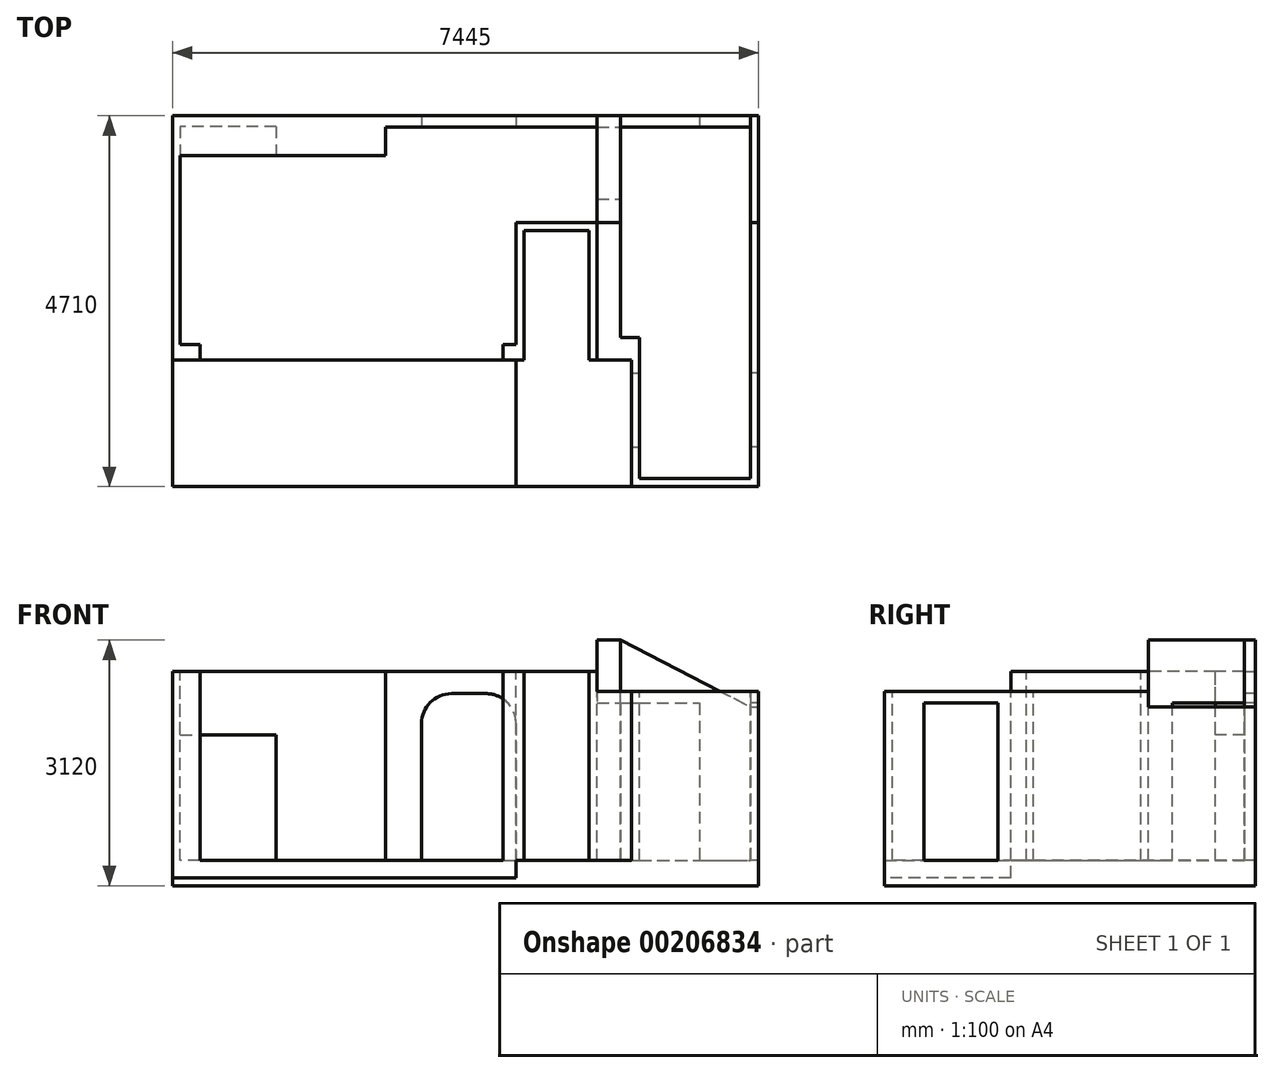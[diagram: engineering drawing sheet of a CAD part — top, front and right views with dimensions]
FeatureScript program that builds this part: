
annotation { "Feature Type Name" : "Feature", "Feature Type Description" : "" }
export const myFeature = defineFeature(function(context is Context, id is Id, definition is map)
    precondition{}
    {
        {
            var Q0;
            Q0=qCreatedBy(makeId("Top.planeOp"),FACE);
            var sketch = newSketch(context, id + "F0", { "sketchPlane" : qUnion([Q0])});
            skLineSegment(sketch, "E0.bottom", {"start": v(-1579.98, 3780.8) * mm, "end": v(5865.02, 3780.8) * mm});
            skLineSegment(sketch, "E0.top", {"start": v(-1579.98, -929.2) * mm, "end": v(5865.02, -929.2) * mm});
            skLineSegment(sketch, "E0.left", {"start": v(-1579.98, 3780.8) * mm, "end": v(-1579.98, -929.2) * mm});
            skLineSegment(sketch, "E0.right", {"start": v(5865.02, 3780.8) * mm, "end": v(5865.02, -929.2) * mm});
            skSolve(sketch);
        }
        {
            var Q0;
            Q0 = qSketchRegion(id + "F0", true);
            extrude(context, id + "F1", {"entities" : qUnion([Q0]), "depth" : 2720 * mm});
        }
        {
            var Q0;
            Q0=makeQuery(id+"F1.opExtrude","CAP_FACE",FACE,{"disambiguationData":[OSD([sQuery(id+"F0.wireOp",EDGE,"E0.bottom"),sQuery(id+"F0.wireOp",EDGE,"E0.top"),sQuery(id+"F0.wireOp",EDGE,"E0.left"),sQuery(id+"F0.wireOp",EDGE,"E0.right")])],"isStart":false});
            var sketch = newSketch(context, id + "F2", { "sketchPlane" : qUnion([Q0])});
            skLineSegment(sketch, "E1.0.0", {"start": v(5865.02, 3780.8) * mm, "end": v(-1579.98, 3780.8) * mm, "construction": true});
            skLineSegment(sketch, "E1.0.1", {"start": v(-1579.98, 3780.8) * mm, "end": v(-1579.98, -929.2) * mm, "construction": true});
            skLineSegment(sketch, "E1.0.2", {"start": v(-1579.98, -929.2) * mm, "end": v(5865.02, -929.2) * mm, "construction": true});
            skLineSegment(sketch, "E1.0.3", {"start": v(5865.02, -929.2) * mm, "end": v(5865.02, 3780.8) * mm, "construction": true});
            skLineSegment(sketch, "E2", {"start": v(-1479.98, 3275.8) * mm, "end": v(-1479.98, 875.8) * mm});
            skLineSegment(sketch, "E3", {"start": v(-1479.98, 875.8) * mm, "end": v(-1229.98, 875.8) * mm});
            skLineSegment(sketch, "E4", {"start": v(-1229.98, 875.8) * mm, "end": v(-1229.98, 675.8) * mm});
            skLineSegment(sketch, "E5", {"start": v(-1229.98, 675.8) * mm, "end": v(2620.02, 675.8) * mm});
            skLineSegment(sketch, "E6", {"start": v(2620.02, 675.8) * mm, "end": v(2620.02, 875.8) * mm});
            skLineSegment(sketch, "E7", {"start": v(2620.02, 875.8) * mm, "end": v(2785.02, 875.8) * mm});
            skLineSegment(sketch, "E8", {"start": v(2785.02, 875.8) * mm, "end": v(2785.02, 2425.8) * mm});
            skLineSegment(sketch, "E9", {"start": v(2785.02, 2425.8) * mm, "end": v(3815.02, 2425.8) * mm});
            skLineSegment(sketch, "E10", {"start": v(4115.02, 963.59) * mm, "end": v(4355.02, 963.59) * mm});
            skLineSegment(sketch, "E11", {"start": v(4355.02, 963.59) * mm, "end": v(4355.02, -829.2) * mm});
            skLineSegment(sketch, "E12", {"start": v(4355.02, -829.2) * mm, "end": v(5765.02, -829.2) * mm});
            skLineSegment(sketch, "E13", {"start": v(5765.02, -829.2) * mm, "end": v(5765.02, -429.2) * mm});
            skLineSegment(sketch, "E14", {"start": v(5765.02, -429.2) * mm, "end": v(5865.02, -429.2) * mm, "construction": true});
            skLineSegment(sketch, "E15", {"start": v(5865.02, -429.2) * mm, "end": v(5865.02, 510.8) * mm, "construction": true});
            skLineSegment(sketch, "E16", {"start": v(5865.02, 510.8) * mm, "end": v(5765.02, 510.8) * mm, "construction": true});
            skLineSegment(sketch, "E17", {"start": v(5765.02, 510.8) * mm, "end": v(5765.02, 3640.8) * mm});
            skLineSegment(sketch, "E18", {"start": v(5765.02, 3640.8) * mm, "end": v(5115.02, 3640.8) * mm});
            skLineSegment(sketch, "E19", {"start": v(5115.02, 3640.8) * mm, "end": v(5115.02, 3780.8) * mm, "construction": true});
            skLineSegment(sketch, "E20", {"start": v(5115.02, 3780.8) * mm, "end": v(4115.02, 3780.8) * mm, "construction": true});
            skLineSegment(sketch, "E21", {"start": v(4115.02, 3780.8) * mm, "end": v(4115.02, 3640.8) * mm, "construction": true});
            skLineSegment(sketch, "E22", {"start": v(4115.02, 3640.8) * mm, "end": v(2785.02, 3640.8) * mm});
            skLineSegment(sketch, "E23", {"start": v(2785.02, 3640.8) * mm, "end": v(2785.02, 3780.8) * mm});
            skLineSegment(sketch, "E24", {"start": v(2785.02, 3780.8) * mm, "end": v(1585.02, 3780.8) * mm, "construction": true});
            skLineSegment(sketch, "E25", {"start": v(1585.02, 3780.8) * mm, "end": v(1585.02, 3640.8) * mm});
            skLineSegment(sketch, "E26", {"start": v(1585.02, 3640.8) * mm, "end": v(1130.02, 3640.8) * mm});
            skLineSegment(sketch, "E27", {"start": v(1130.02, 3640.8) * mm, "end": v(1130.02, 3275.8) * mm});
            skLineSegment(sketch, "E28", {"start": v(1130.02, 3275.8) * mm, "end": v(-1479.98, 3275.8) * mm});
            skPoint(sketch, "E29.orphan", {"position": v(-1479.98, 3640.8) * mm});
            skLineSegment(sketch, "E30", {"start": v(2785.02, 3710.8) * mm, "end": v(2785.02, 1947.94) * mm, "construction": true});
            skLineSegment(sketch, "E31", {"start": v(3815.02, 2425.8) * mm, "end": v(3815.02, 2725.8) * mm});
            skLineSegment(sketch, "E32", {"start": v(3815.02, 2725.8) * mm, "end": v(4115.02, 2725.8) * mm});
            skLineSegment(sketch, "E33", {"start": v(4115.02, 2725.8) * mm, "end": v(4115.02, 963.59) * mm});
            skLineSegment(sketch, "E34", {"start": v(1585.02, 3640.8) * mm, "end": v(2785.02, 3640.8) * mm});
            skLineSegment(sketch, "E35", {"start": v(4115.02, 3640.8) * mm, "end": v(5115.02, 3640.8) * mm});
            skLineSegment(sketch, "E36", {"start": v(5765.02, 510.8) * mm, "end": v(5765.02, -429.2) * mm});
            skSolve(sketch);
        }
        {
            var Q0;
            Q0 = qSketchRegion(id + "F2", true);
            extrude(context, id + "F3", {"entities" : qUnion([Q0]), "operationType" : NewBodyOperationType.REMOVE, "oppositeDirection" : true, "depth" : 2400 * mm});
        }
        {
            var Q0;
            Q0=makeQuery(id+"F3.boolean.opBoolean","COPY",FACE,{"derivedFrom":makeQuery(id+"F3.opExtrude","SWEPT_FACE",FACE,{"disambiguationData":[OSD([sQuery(id+"F2.wireOp",EDGE,"E28")])]})});
            var sketch = newSketch(context, id + "F4", { "sketchPlane" : qUnion([Q0])});
            skLineSegment(sketch, "E37.bottom", {"start": v(-1479.98, 320) * mm, "end": v(-259.98, 320) * mm});
            skLineSegment(sketch, "E37.top", {"start": v(-1479.98, 1915) * mm, "end": v(-259.98, 1915) * mm});
            skLineSegment(sketch, "E37.left", {"start": v(-1479.98, 320) * mm, "end": v(-1479.98, 1915) * mm});
            skLineSegment(sketch, "E37.right", {"start": v(-259.98, 320) * mm, "end": v(-259.98, 1915) * mm});
            skSolve(sketch);
        }
        {
            var Q0;
            Q0 = qSketchRegion(id + "F4", true);
            extrude(context, id + "F5", {"entities" : qUnion([Q0]), "operationType" : NewBodyOperationType.REMOVE, "oppositeDirection" : true, "depth" : 370 * mm});
        }
        {
            var Q0;
            Q0=makeQuery(id+"F3.boolean.opBoolean","COPY",FACE,{"derivedFrom":makeQuery(id+"F3.opExtrude","SWEPT_FACE",FACE,{"disambiguationData":[OSD([sQuery(id+"F2.wireOp",EDGE,"E18"),sQuery(id+"F2.wireOp",EDGE,"E22"),sQuery(id+"F2.wireOp",EDGE,"E26"),sQuery(id+"F2.wireOp",EDGE,"E34"),sQuery(id+"F2.wireOp",EDGE,"E35")])]})});
            var sketch = newSketch(context, id + "F6", { "sketchPlane" : qUnion([Q0])});
            skPoint(sketch, "E38.0", {"position": v(1585.02, 2720) * mm});
            skPoint(sketch, "E39.0", {"position": v(2785.02, 2720) * mm});
            skPoint(sketch, "E40.0", {"position": v(4115.02, 2720) * mm});
            skPoint(sketch, "E41.0", {"position": v(5115.02, 2720) * mm});
            skLineSegment(sketch, "E42.top", {"start": v(1585.02, 320) * mm, "end": v(2785.02, 320) * mm});
            skLineSegment(sketch, "E42.left", {"start": v(1585.02, 2440) * mm, "end": v(1585.02, 320) * mm});
            skLineSegment(sketch, "E42.right", {"start": v(2785.02, 2440) * mm, "end": v(2785.02, 320) * mm});
            skLineSegment(sketch, "E43.top", {"start": v(4115.02, 320) * mm, "end": v(5115.02, 320) * mm});
            skLineSegment(sketch, "E43.left", {"start": v(4115.02, 2320) * mm, "end": v(4115.02, 320) * mm});
            skLineSegment(sketch, "E43.right", {"start": v(5115.02, 2320) * mm, "end": v(5115.02, 320) * mm});
            skLineSegment(sketch, "E44", {"start": v(1585.02, 2440) * mm, "end": v(2785.02, 2440) * mm});
            skLineSegment(sketch, "E45", {"start": v(4115.02, 2320) * mm, "end": v(5115.02, 2320) * mm});
            skSolve(sketch);
        }
        {
            var Q0;
            Q0 = qSketchRegion(id + "F6", true);
            extrude(context, id + "F7", {"entities" : qUnion([Q0]), "operationType" : NewBodyOperationType.REMOVE, "endBound" : BoundingType.UP_TO_NEXT, "oppositeDirection" : true, "depth" : 25 * mm});
        }
        {
            var Q0;
            Q0=makeQuery(id+"F7.boolean.opBoolean","COPY",EDGE,{"derivedFrom":makeQuery(id+"F7.opExtrude","SWEPT_EDGE",EDGE,{"disambiguationData":[OSD([sQuery(id+"F6.wireOp",EDGE,"E42.left"),sQuery(id+"F6.wireOp",EDGE,"E44")])]})});
            var Q1;
            Q1=makeQuery(id+"F7.boolean.opBoolean","COPY",EDGE,{"derivedFrom":makeQuery(id+"F7.opExtrude","SWEPT_EDGE",EDGE,{"disambiguationData":[OSD([sQuery(id+"F6.wireOp",EDGE,"E42.right"),sQuery(id+"F6.wireOp",EDGE,"E44")])]})});
            fillet(context, id + "F8", {"entities" : qUnion([Q0, Q1]), "radius" : 380 * mm, "tangentPropagation" : true, "allowEdgeOverflow" : false});
        }
        {
            var Q0;
            Q0=makeQuery(id+"F2.imprint","IMPRINT",FACE,{"disambiguationData":[TD([[makeQuery(id+"F2.imprint","IMPRINT",EDGE,{"derivedFrom":sQuery(id+"F2.wireOp",EDGE,"E2")}),-1.0]])]});
            var sketch = newSketch(context, id + "F9", { "sketchPlane" : qUnion([Q0])});
            skPoint(sketch, "E46.0", {"position": v(-1579.98, -929.2) * mm});
            skLineSegment(sketch, "E47.0", {"start": v(-1229.98, 675.8) * mm, "end": v(2620.02, 675.8) * mm});
            skLineSegment(sketch, "E48.0", {"start": v(4355.02, 963.59) * mm, "end": v(4355.02, -829.2) * mm, "construction": true});
            skLineSegment(sketch, "E49.bottom", {"start": v(-1579.98, -929.2) * mm, "end": v(4255.02, -929.2) * mm});
            skLineSegment(sketch, "E49.top", {"start": v(-1579.98, 675.8) * mm, "end": v(4255.02, 675.8) * mm});
            skLineSegment(sketch, "E49.left", {"start": v(-1579.98, -929.2) * mm, "end": v(-1579.98, 675.8) * mm});
            skLineSegment(sketch, "E49.right", {"start": v(4255.02, -929.2) * mm, "end": v(4255.02, 675.8) * mm});
            skLineSegment(sketch, "E50.0", {"start": v(2785.02, 875.8) * mm, "end": v(2785.02, 2425.8) * mm, "construction": true});
            skLineSegment(sketch, "E51.0", {"start": v(2785.02, 2425.8) * mm, "end": v(3815.02, 2425.8) * mm, "construction": true});
            skLineSegment(sketch, "E52.top", {"start": v(2885.02, 2325.8) * mm, "end": v(3715.02, 2325.8) * mm});
            skLineSegment(sketch, "E52.left", {"start": v(2885.02, 675.8) * mm, "end": v(2885.02, 2325.8) * mm});
            skLineSegment(sketch, "E52.right", {"start": v(3715.02, 675.8) * mm, "end": v(3715.02, 2325.8) * mm});
            skSolve(sketch);
        }
        {
            var Q0;
            Q0 = qSketchRegion(id + "F9", true);
            extrude(context, id + "F10", {"entities" : qUnion([Q0]), "operationType" : NewBodyOperationType.REMOVE, "oppositeDirection" : true, "depth" : 2400 * mm});
        }
        {
            var Q0;
            Q0=makeQuery(id+"F3.boolean.opBoolean","COPY",FACE,{"derivedFrom":makeQuery(id+"F3.opExtrude","SWEPT_FACE",FACE,{"disambiguationData":[OSD([sQuery(id+"F2.wireOp",EDGE,"E13"),sQuery(id+"F2.wireOp",EDGE,"E17"),sQuery(id+"F2.wireOp",EDGE,"E36")])]})});
            var sketch = newSketch(context, id + "F11", { "sketchPlane" : qUnion([Q0])});
            skPoint(sketch, "E53.0", {"position": v(-510.8, 2720) * mm});
            skPoint(sketch, "E54.0", {"position": v(429.2, 2720) * mm});
            skLineSegment(sketch, "E55.top", {"start": v(-510.8, 320) * mm, "end": v(429.2, 320) * mm});
            skLineSegment(sketch, "E55.left", {"start": v(-510.8, 2320) * mm, "end": v(-510.8, 320) * mm});
            skLineSegment(sketch, "E55.right", {"start": v(429.2, 2320) * mm, "end": v(429.2, 320) * mm});
            skLineSegment(sketch, "E56", {"start": v(-510.8, 2320) * mm, "end": v(429.2, 2320) * mm});
            skSolve(sketch);
        }
        {
            var Q0;
            Q0 = qSketchRegion(id + "F11", true);
            extrude(context, id + "F12", {"entities" : qUnion([Q0]), "operationType" : NewBodyOperationType.REMOVE, "endBound" : BoundingType.UP_TO_NEXT, "oppositeDirection" : true, "depth" : 25 * mm});
        }
        {
            var Q0;
            Q0 = qSketchRegion(id + "F11", true);
            var Q1;
            Q1=makeQuery(id+"F10.boolean.opBoolean","COPY",FACE,{"derivedFrom":makeQuery(id+"F10.opExtrude","SWEPT_FACE",FACE,{"disambiguationData":[OSD([sQuery(id+"F9.wireOp",EDGE,"E49.right")])]})});
            extrude(context, id + "F13", {"entities" : qUnion([Q0]), "operationType" : NewBodyOperationType.REMOVE, "endBound" : BoundingType.UP_TO_SURFACE, "endBoundEntityFace" : qUnion([Q1]), "depth" : 25 * mm});
        }
        {
            var Q0;
            Q0=makeQuery(id+"F3.boolean.opBoolean","COPY",FACE,{"derivedFrom":makeQuery(id+"F3.opExtrude","SWEPT_FACE",FACE,{"disambiguationData":[OSD([sQuery(id+"F2.wireOp",EDGE,"E33")])]})});
            var sketch = newSketch(context, id + "F14", { "sketchPlane" : qUnion([Q0])});
            skPoint(sketch, "E57.0", {"position": v(3640.8, 2320) * mm});
            skLineSegment(sketch, "E58.bottom", {"start": v(3640.8, 2320) * mm, "end": v(2725.8, 2320) * mm});
            skLineSegment(sketch, "E58.top", {"start": v(3640.8, 2720) * mm, "end": v(2725.8, 2720) * mm});
            skLineSegment(sketch, "E58.left", {"start": v(3640.8, 2320) * mm, "end": v(3640.8, 2720) * mm});
            skLineSegment(sketch, "E58.right", {"start": v(2725.8, 2320) * mm, "end": v(2725.8, 2720) * mm});
            skSolve(sketch);
        }
        {
            var Q0;
            Q0 = qSketchRegion(id + "F14", true);
            var Q1;
            Q1=makeQuery(id+"F3.boolean.opBoolean","COPY",FACE,{"derivedFrom":makeQuery(id+"F3.opExtrude","SWEPT_FACE",FACE,{"disambiguationData":[OSD([sQuery(id+"F2.wireOp",EDGE,"E31")])]})});
            extrude(context, id + "F15", {"entities" : qUnion([Q0]), "operationType" : NewBodyOperationType.ADD, "endBound" : BoundingType.UP_TO_SURFACE, "oppositeDirection" : true, "endBoundEntityFace" : qUnion([Q1]), "depth" : 25 * mm});
        }
        {
            var Q0;
            Q0=makeQuery(id+"F2.imprint","IMPRINT",FACE,{"disambiguationData":[TD([[makeQuery(id+"F2.imprint","IMPRINT",EDGE,{"derivedFrom":sQuery(id+"F2.wireOp",EDGE,"E2")}),-1.0]])]});
            var sketch = newSketch(context, id + "F16", { "sketchPlane" : qUnion([Q0])});
            skPoint(sketch, "E59.0", {"position": v(4115.02, 3640.8) * mm});
            skPoint(sketch, "E60.0", {"position": v(3815.02, 2425.8) * mm});
            skLineSegment(sketch, "E61.top", {"start": v(4115.02, 2425.8) * mm, "end": v(3815.02, 2425.8) * mm});
            skLineSegment(sketch, "E61.left", {"start": v(4115.02, 3640.8) * mm, "end": v(4115.02, 2425.8) * mm});
            skLineSegment(sketch, "E61.right", {"start": v(3815.02, 3640.8) * mm, "end": v(3815.02, 2425.8) * mm});
            skPoint(sketch, "E62.0", {"position": v(5865.02, 3780.8) * mm});
            skPoint(sketch, "E63.0", {"position": v(5765.02, 3640.8) * mm});
            skLineSegment(sketch, "E64.top", {"start": v(5765.02, 2425.8) * mm, "end": v(5865.02, 2425.8) * mm});
            skLineSegment(sketch, "E64.left", {"start": v(5765.02, 3640.8) * mm, "end": v(5765.02, 2425.8) * mm});
            skLineSegment(sketch, "E64.right", {"start": v(5865.02, 3640.8) * mm, "end": v(5865.02, 2425.8) * mm});
            skLineSegment(sketch, "E65.bottom", {"start": v(4115.02, 3640.8) * mm, "end": v(5765.02, 3640.8) * mm});
            skLineSegment(sketch, "E65.top", {"start": v(3815.02, 3780.8) * mm, "end": v(5865.02, 3780.8) * mm});
            skLineSegment(sketch, "E65.left", {"start": v(3815.02, 3640.8) * mm, "end": v(3815.02, 3780.8) * mm});
            skLineSegment(sketch, "E65.right", {"start": v(5865.02, 3640.8) * mm, "end": v(5865.02, 3780.8) * mm});
            skSolve(sketch);
        }
        {
            var Q0;
            Q0 = qSketchRegion(id + "F16", true);
            extrude(context, id + "F17", {"entities" : qUnion([Q0]), "operationType" : NewBodyOperationType.ADD, "depth" : 400 * mm});
        }
        {
            var Q0;
            Q0=makeQuery(id+"F1.opExtrude","SWEPT_FACE",FACE,{"disambiguationData":[OSD([sQuery(id+"F0.wireOp",EDGE,"E0.right")])]});
            var sketch = newSketch(context, id + "F18", { "sketchPlane" : qUnion([Q0])});
            skPoint(sketch, "E66.0", {"position": v(2425.8, 2720) * mm});
            skLineSegment(sketch, "E67.bottom", {"start": v(2425.8, 2720) * mm, "end": v(-929.2, 2720) * mm});
            skLineSegment(sketch, "E67.top", {"start": v(2425.8, 2470) * mm, "end": v(-929.2, 2470) * mm});
            skLineSegment(sketch, "E67.left", {"start": v(2425.8, 2720) * mm, "end": v(2425.8, 2470) * mm});
            skLineSegment(sketch, "E67.right", {"start": v(-929.2, 2720) * mm, "end": v(-929.2, 2470) * mm});
            skSolve(sketch);
        }
        {
            var Q0;
            Q0 = qSketchRegion(id + "F18", true);
            extrude(context, id + "F19", {"entities" : qUnion([Q0]), "operationType" : NewBodyOperationType.REMOVE, "oppositeDirection" : true, "depth" : 2049 * mm});
        }
        {
            var Q0;
            Q0=makeQuery(id+"F19.boolean.opBoolean","MERGE",FACE,{"derivedFrom":[makeQuery(id+"F17.opExtrude","SWEPT_FACE",FACE,{"disambiguationData":[OSD([sQuery(id+"F16.wireOp",EDGE,"E64.top")])]}),makeQuery(id+"F19.opExtrude","SWEPT_FACE",FACE,{"disambiguationData":[OSD([sQuery(id+"F18.wireOp",EDGE,"E67.left")])]})]});
            var sketch = newSketch(context, id + "F20", { "sketchPlane" : qUnion([Q0])});
            skPoint(sketch, "E68.0", {"position": v(5765.02, 2470) * mm});
            skPoint(sketch, "E69.0", {"position": v(4115.02, 3120) * mm});
            skPoint(sketch, "E70", {"position": v(5765.02, 2270) * mm});
            skLineSegment(sketch, "E71", {"start": v(4115.02, 3120) * mm, "end": v(5765.02, 2270) * mm});
            skLineSegment(sketch, "E72", {"start": v(5765.02, 2270) * mm, "end": v(5865.02, 2270) * mm});
            skLineSegment(sketch, "E73", {"start": v(5865.02, 2270) * mm, "end": v(5865.02, 3120) * mm});
            skLineSegment(sketch, "E74", {"start": v(5865.02, 3120) * mm, "end": v(4115.02, 3120) * mm});
            skSolve(sketch);
        }
        {
            var Q0;
            Q0 = qSketchRegion(id + "F20", true);
            var Q1;
            Q1=makeQuery(id+"F17.boolean.opBoolean","MERGE",FACE,{"derivedFrom":[makeQuery(id+"F1.opExtrude","SWEPT_FACE",FACE,{"disambiguationData":[OSD([sQuery(id+"F0.wireOp",EDGE,"E0.bottom")])]}),makeQuery(id+"F17.opExtrude","SWEPT_FACE",FACE,{"disambiguationData":[OSD([sQuery(id+"F16.wireOp",EDGE,"E65.top")])]})]});
            extrude(context, id + "F21", {"entities" : qUnion([Q0]), "operationType" : NewBodyOperationType.REMOVE, "endBound" : BoundingType.UP_TO_SURFACE, "oppositeDirection" : true, "endBoundEntityFace" : qUnion([Q1]), "depth" : 1340 * mm});
        }
        {
            var Q0;
            {var subQ0=sQuery(id+"F11.wireOp",EDGE,"E55.top");Q0=makeQuery(id+"F13.boolean.opBoolean","MERGE",FACE,{"derivedFrom":[makeQuery(id+"F12.boolean.opBoolean","MERGE",FACE,{"derivedFrom":[makeQuery(id+"F10.boolean.opBoolean","MERGE",FACE,{"derivedFrom":[makeQuery(id+"F7.boolean.opBoolean","MERGE",FACE,{"derivedFrom":[makeQuery(id+"F5.boolean.opBoolean","MERGE",FACE,{"derivedFrom":[makeQuery(id+"F3.boolean.opBoolean","COPY",FACE,{"derivedFrom":makeQuery(id+"F3.opExtrude","CAP_FACE",FACE,{"disambiguationData":[OSD([sQuery(id+"F2.wireOp",EDGE,"E2"),sQuery(id+"F2.wireOp",EDGE,"E3"),sQuery(id+"F2.wireOp",EDGE,"E4"),sQuery(id+"F2.wireOp",EDGE,"E5"),sQuery(id+"F2.wireOp",EDGE,"E6"),sQuery(id+"F2.wireOp",EDGE,"E7"),sQuery(id+"F2.wireOp",EDGE,"E8"),sQuery(id+"F2.wireOp",EDGE,"E9"),sQuery(id+"F2.wireOp",EDGE,"E10"),sQuery(id+"F2.wireOp",EDGE,"E11"),sQuery(id+"F2.wireOp",EDGE,"E12"),sQuery(id+"F2.wireOp",EDGE,"E13"),sQuery(id+"F2.wireOp",EDGE,"E17"),sQuery(id+"F2.wireOp",EDGE,"E18"),sQuery(id+"F2.wireOp",EDGE,"E22"),sQuery(id+"F2.wireOp",EDGE,"E26"),sQuery(id+"F2.wireOp",EDGE,"E27"),sQuery(id+"F2.wireOp",EDGE,"E28"),sQuery(id+"F2.wireOp",EDGE,"E31"),sQuery(id+"F2.wireOp",EDGE,"E32"),sQuery(id+"F2.wireOp",EDGE,"E33"),sQuery(id+"F2.wireOp",EDGE,"E34"),sQuery(id+"F2.wireOp",EDGE,"E35"),sQuery(id+"F2.wireOp",EDGE,"E36")])],"isStart":false})}),makeQuery(id+"F5.opExtrude","SWEPT_FACE",FACE,{"disambiguationData":[OSD([sQuery(id+"F4.wireOp",EDGE,"E37.bottom")])]})]}),makeQuery(id+"F7.opExtrude","SWEPT_FACE",FACE,{"disambiguationData":[OSD([sQuery(id+"F6.wireOp",EDGE,"E42.top")])]}),makeQuery(id+"F7.opExtrude","SWEPT_FACE",FACE,{"disambiguationData":[OSD([sQuery(id+"F6.wireOp",EDGE,"E43.top")])]})]}),makeQuery(id+"F10.opExtrude","CAP_FACE",FACE,{"disambiguationData":[OSD([sQuery(id+"F9.wireOp",EDGE,"E49.bottom"),sQuery(id+"F9.wireOp",EDGE,"E49.top"),sQuery(id+"F9.wireOp",EDGE,"E49.left"),sQuery(id+"F9.wireOp",EDGE,"E49.right"),sQuery(id+"F9.wireOp",EDGE,"E52.top"),sQuery(id+"F9.wireOp",EDGE,"E52.left"),sQuery(id+"F9.wireOp",EDGE,"E52.right")])],"isStart":false})]}),makeQuery(id+"F12.opExtrude","SWEPT_FACE",FACE,{"disambiguationData":[OSD([subQ0])]})]}),makeQuery(id+"F13.opExtrude","SWEPT_FACE",FACE,{"disambiguationData":[OSD([subQ0])]})]});}
            var sketch = newSketch(context, id + "F22", { "sketchPlane" : qUnion([Q0])});
            skLineSegment(sketch, "E75.bottom", {"start": v(-1579.98, -929.2) * mm, "end": v(2785.02, -929.2) * mm});
            skLineSegment(sketch, "E75.top", {"start": v(-1579.98, 675.8) * mm, "end": v(2785.02, 675.8) * mm});
            skLineSegment(sketch, "E75.left", {"start": v(-1579.98, -929.2) * mm, "end": v(-1579.98, 675.8) * mm});
            skLineSegment(sketch, "E75.right", {"start": v(2785.02, -929.2) * mm, "end": v(2785.02, 675.8) * mm});
            skSolve(sketch);
        }
        {
            var Q0;
            Q0 = qSketchRegion(id + "F22", true);
            extrude(context, id + "F23", {"entities" : qUnion([Q0]), "operationType" : NewBodyOperationType.REMOVE, "oppositeDirection" : true, "depth" : 220 * mm});
        }
    });
